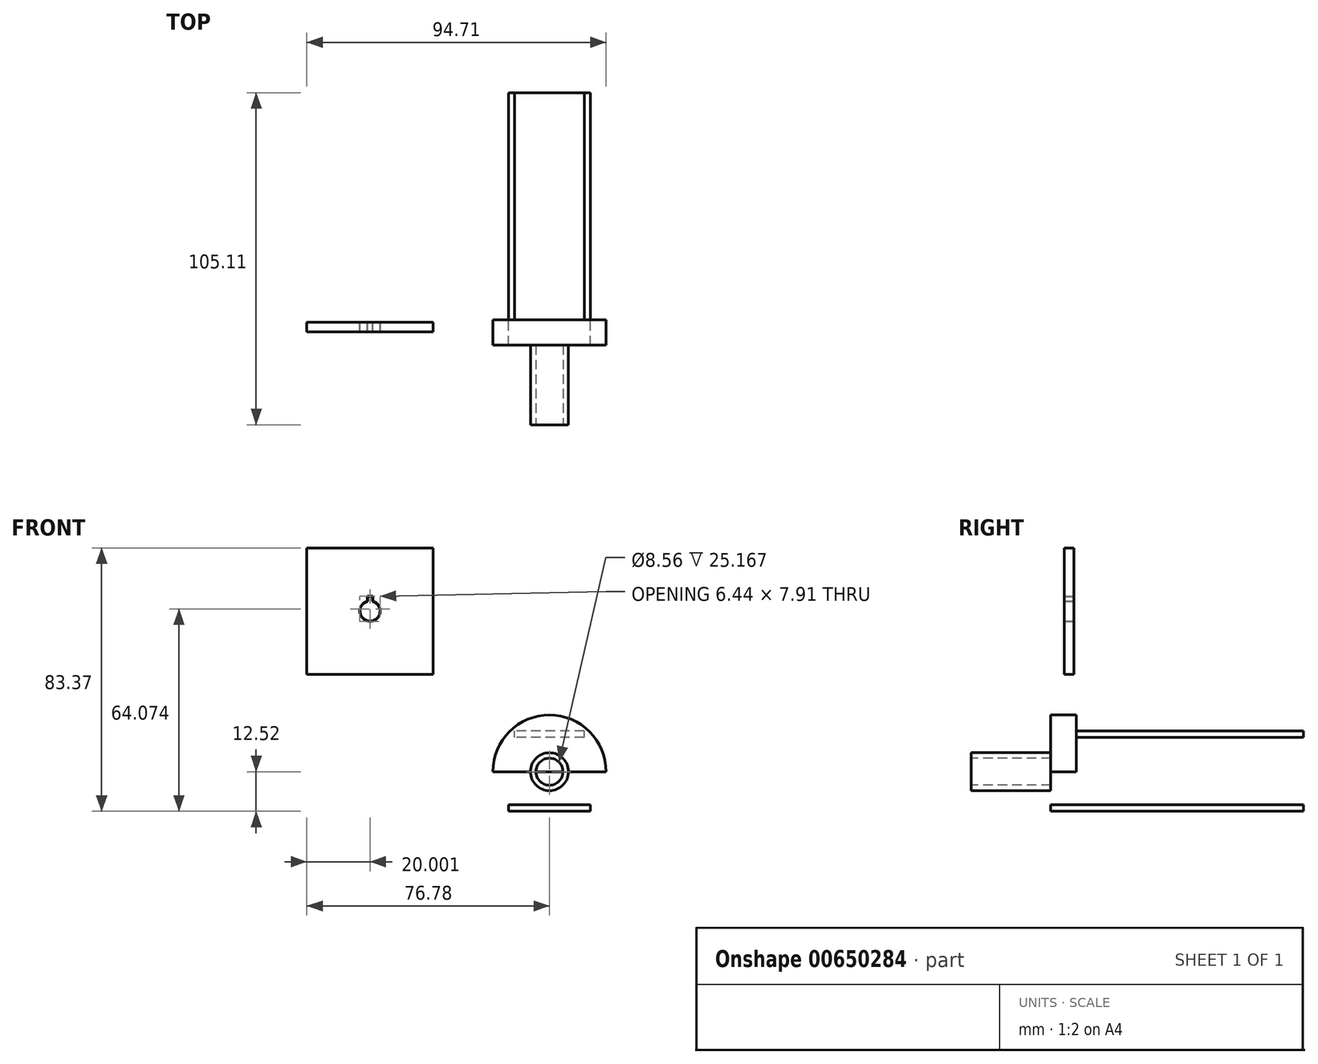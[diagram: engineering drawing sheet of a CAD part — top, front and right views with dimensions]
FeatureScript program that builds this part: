
annotation { "Feature Type Name" : "Feature", "Feature Type Description" : "" }
export const myFeature = defineFeature(function(context is Context, id is Id, definition is map)
    precondition{}
    {
        {
            var Q0;
            Q0=qCreatedBy(makeId("Right.planeOp"),FACE);
            var sketch = newSketch(context, id + "F0", { "sketchPlane" : qUnion([Q0])});
            skLineSegment(sketch, "E0", {"start": v(-43.45, 0) * mm, "end": v(66.43, 0) * mm, "construction": true});
            skLineSegment(sketch, "E1.bottom", {"start": v(-32.44, 4.28) * mm, "end": v(-7.28, 4.28) * mm});
            skLineSegment(sketch, "E1.top", {"start": v(-32.44, 6) * mm, "end": v(-7.28, 6) * mm});
            skLineSegment(sketch, "E1.left", {"start": v(-32.44, 4.28) * mm, "end": v(-32.44, 6) * mm});
            skLineSegment(sketch, "E1.right", {"start": v(-7.28, 4.28) * mm, "end": v(-7.28, 6) * mm});
            skLineSegment(sketch, "E2.bottom", {"start": v(-7.28, 0) * mm, "end": v(0.72, 0) * mm});
            skLineSegment(sketch, "E2.top", {"start": v(-7.28, 17.93) * mm, "end": v(0.72, 17.93) * mm});
            skLineSegment(sketch, "E2.left", {"start": v(-7.28, 0) * mm, "end": v(-7.28, 17.93) * mm});
            skLineSegment(sketch, "E2.right", {"start": v(0.72, 0) * mm, "end": v(0.72, 17.93) * mm});
            skLineSegment(sketch, "E3.bottom", {"start": v(-7.28, -10.52) * mm, "end": v(72.67, -10.52) * mm});
            skLineSegment(sketch, "E3.top", {"start": v(-7.28, -12.52) * mm, "end": v(72.67, -12.52) * mm});
            skLineSegment(sketch, "E3.left", {"start": v(-7.28, -10.52) * mm, "end": v(-7.28, -12.52) * mm});
            skLineSegment(sketch, "E3.right", {"start": v(72.67, -10.52) * mm, "end": v(72.67, -12.52) * mm});
            skLineSegment(sketch, "E4.bottom", {"start": v(0.72, 12.92) * mm, "end": v(72.67, 12.92) * mm});
            skLineSegment(sketch, "E4.top", {"start": v(0.72, 10.92) * mm, "end": v(72.67, 10.92) * mm});
            skLineSegment(sketch, "E4.left", {"start": v(0.72, 12.92) * mm, "end": v(0.72, 10.92) * mm});
            skLineSegment(sketch, "E4.right", {"start": v(72.67, 12.92) * mm, "end": v(72.67, 10.92) * mm});
            skLineSegment(sketch, "E5.bottom", {"start": v(10.23, 10.92) * mm, "end": v(65.04, 10.92) * mm});
            skLineSegment(sketch, "E5.top", {"start": v(10.23, -10.52) * mm, "end": v(65.04, -10.52) * mm});
            skLineSegment(sketch, "E5.left", {"start": v(10.23, 10.92) * mm, "end": v(10.23, -10.52) * mm});
            skLineSegment(sketch, "E5.right", {"start": v(65.04, 10.92) * mm, "end": v(65.04, -10.52) * mm});
            skLineSegment(sketch, "E6.top", {"start": v(-7.28, -10.52) * mm, "end": v(0.72, -10.52) * mm});
            skLineSegment(sketch, "E6.left", {"start": v(-7.28, 0) * mm, "end": v(-7.28, -10.52) * mm});
            skLineSegment(sketch, "E6.right", {"start": v(0.72, 0) * mm, "end": v(0.72, -10.52) * mm});
            skSolve(sketch);
        }
        {
            var Q0;
            {var subQ0=sQuery(id+"F0.wireOp",EDGE,"E1.bottom");Q0=makeQuery(id+"F0.imprint","IMPRINT",FACE,{"disambiguationData":[TD([[makeQuery(id+"F0.imprint","IMPRINT",EDGE,{"derivedFrom":subQ0}),1.0]])]});}
            var Q1;
            Q1=sQuery(id+"F0.wireOp",EDGE,"E0");
            revolve(context, id + "F1", {"entities" : qUnion([Q0]), "axis" : qUnion([Q1]), "revolveType" : RevolveType.FULL});
        }
        {
            var Q0;
            {var subQ2=sQuery(id+"F0.wireOp",EDGE,"E2.top");Q0=makeQuery(id+"F0.imprint","IMPRINT",FACE,{"disambiguationData":[TD([[makeQuery(id+"F0.imprint","IMPRINT",EDGE,{"derivedFrom":subQ2}),-1.0]])]});}
            var Q1;
            Q1=sQuery(id+"F0.wireOp",EDGE,"E0");
            revolve(context, id + "F2", {"operationType" : NewBodyOperationType.ADD, "entities" : qUnion([Q0]), "axis" : qUnion([Q1]), "revolveType" : RevolveType.SYMMETRIC, "angle" : 180 * degree});
        }
        {
            var Q0;
            Q0=makeQuery(id+"F0.imprint","IMPRINT",FACE,{"disambiguationData":[TD([[makeQuery(id+"F0.imprint","IMPRINT",EDGE,{"derivedFrom":sQuery(id+"F0.wireOp",EDGE,"E3.top")}),1.0]])]});
            extrude(context, id + "F3", {"entities" : qUnion([Q0]), "endBound" : BoundingType.SYMMETRIC, "depth" : 26 * mm, "offsetDistance" : 25 * mm});
        }
        {
            var Q0;
            Q0=makeQuery(id+"F0.imprint","IMPRINT",FACE,{"disambiguationData":[TD([[makeQuery(id+"F0.imprint","IMPRINT",EDGE,{"derivedFrom":sQuery(id+"F0.wireOp",EDGE,"E4.bottom")}),-1.0]])]});
            extrude(context, id + "F4", {"entities" : qUnion([Q0]), "operationType" : NewBodyOperationType.ADD, "endBound" : BoundingType.SYMMETRIC, "depth" : 22 * mm, "offsetDistance" : 25 * mm});
        }
        {
            var Q0;
            Q0=qCreatedBy(makeId("Front.planeOp"),FACE);
            var sketch = newSketch(context, id + "F5", { "sketchPlane" : qUnion([Q0])});
            skLineSegment(sketch, "E7.bottom", {"start": v(-36.78, 70.85) * mm, "end": v(-76.78, 70.85) * mm});
            skLineSegment(sketch, "E7.top", {"start": v(-36.78, 30.85) * mm, "end": v(-76.78, 30.85) * mm});
            skLineSegment(sketch, "E7.left", {"start": v(-36.78, 70.85) * mm, "end": v(-36.78, 30.85) * mm});
            skLineSegment(sketch, "E7.right", {"start": v(-76.78, 70.85) * mm, "end": v(-76.78, 30.85) * mm});
            skPoint(sketch, "E7.middle", {"position": v(-56.78, 50.85) * mm});
            skArc(sketch, "E8", {"start": v(-57.63, 53.99) * mm, "mid": v(-56.78, 47.6) * mm, "end": v(-55.93, 53.99) * mm});
            skLineSegment(sketch, "E9.top", {"start": v(-57.63, 55.5) * mm, "end": v(-55.93, 55.5) * mm});
            skLineSegment(sketch, "E9.left", {"start": v(-57.63, 53.99) * mm, "end": v(-57.63, 55.5) * mm});
            skLineSegment(sketch, "E9.right", {"start": v(-55.93, 53.99) * mm, "end": v(-55.93, 55.5) * mm});
            skArc(sketch, "E10.0", {"start": v(-57.53, 53.9) * mm, "mid": v(-56.78, 47.7) * mm, "end": v(-56.03, 53.9) * mm});
            skLineSegment(sketch, "E10.1", {"start": v(-57.53, 53.9) * mm, "end": v(-57.53, 55.4) * mm});
            skLineSegment(sketch, "E10.2", {"start": v(-57.53, 55.4) * mm, "end": v(-56.03, 55.4) * mm});
            skLineSegment(sketch, "E10.3", {"start": v(-56.03, 53.9) * mm, "end": v(-56.03, 55.4) * mm});
            skLineSegment(sketch, "E11", {"start": v(-56.78, 50.85) * mm, "end": v(-56.78, 54.96) * mm, "construction": true});
            skSolve(sketch);
        }
        {
            var Q0;
            Q0 = qSketchRegion(id + "F5", true);
            var Q1;
            Q1=makeQuery(id+"F5.imprint","IMPRINT",FACE,{"disambiguationData":[TD([[makeQuery(id+"F5.imprint","IMPRINT",EDGE,{"derivedFrom":sQuery(id+"F5.wireOp",EDGE,"E10.0")}),1.0]])]});
            extrude(context, id + "F6", {"entities" : qUnion([Q0, Q1]), "depth" : 3 * mm, "offsetDistance" : 25 * mm});
        }
    });
